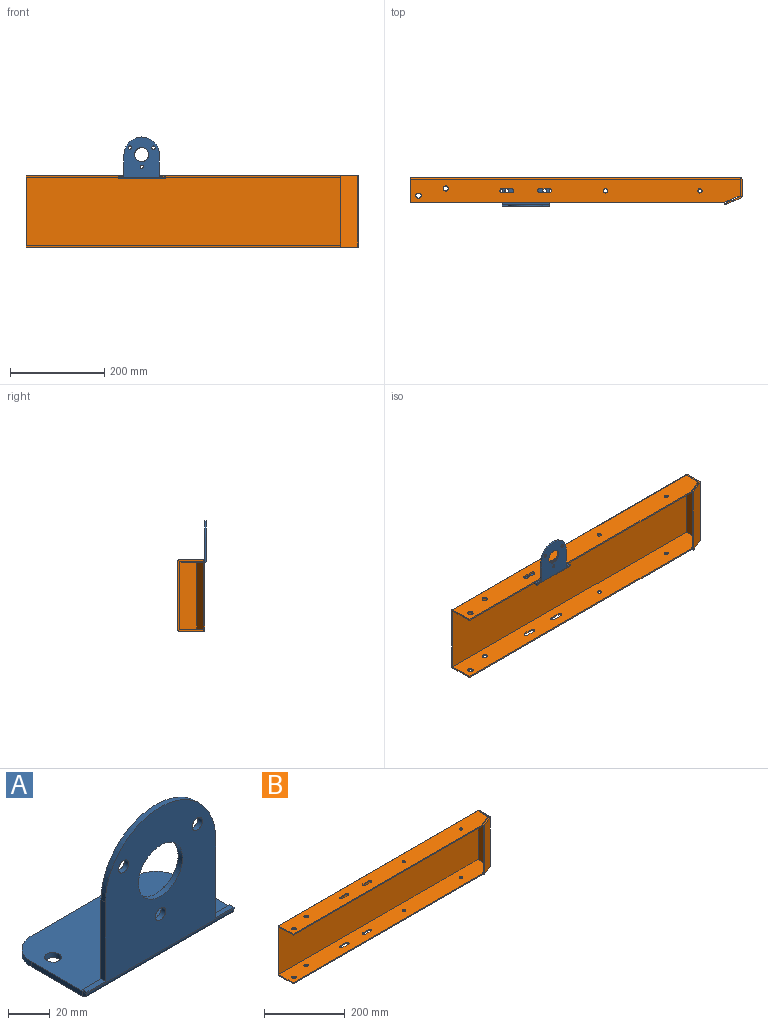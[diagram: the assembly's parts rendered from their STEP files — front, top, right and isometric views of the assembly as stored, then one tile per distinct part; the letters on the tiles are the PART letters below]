
ASSEMBLY  parts=2 mates=1
PART A: 26 faces, bbox 100x53x88 mm
  f0: plane 12.5x3mm, normal (0,0,1), area 37.5mm2, adj f1,f10,f11,f12
  f1: plane 3x0.99mm, normal (-1,0,0), area 3mm2, adj f0,f11,f12,f23
  f2: plane 3x0.99mm, normal (1,0,0), area 3mm2, adj f3,f11,f12,f22
  f3: plane 12.5x3mm, normal (0,0,1), area 37.5mm2, adj f2,f4,f11,f12
  f4: plane 46.5x3mm, normal (1,0,0), area 139.5mm2, adj f3,f5,f11,f12
  f5: cylinder r=37.5mm len=75mm, axis (0,-1,0), area 353.4mm2, adj f4,f10,f11,f12
  f6: cylinder r=15mm len=30mm, axis (0,-1,0), area 282.7mm2, adj f11,f12
  f7: cylinder r=3.5mm len=7mm, axis (0,-1,0), area 66mm2, adj f11,f12
  f8: cylinder r=3.5mm len=7mm, axis (0,-1,0), area 66mm2, adj f11,f12
  f9: cylinder r=3.5mm len=7mm, axis (0,-1,0), area 66mm2, adj f11,f12
  f10: plane 46.5x3mm, normal (-1,0,0), area 139.5mm2, adj f0,f5,f11,f12
  f11: plane 100x84.99mm, normal (0,-1,0), area 4973.1mm2, adj f0,f1,f2,f3,f4,f5,f6,f7
  f12: plane 100x84.99mm, normal (0,1,0), area 4973.1mm2, adj f0,f1,f2,f3,f4,f5,f6,f7
  f13: plane 70x3mm, normal (0,1,0), area 210mm2, adj f18,f19,f20,f21
  f14: plane 34.99x3mm, normal (1,0,0), area 105mm2, adj f18,f19,f20,f22
  f15: cylinder r=4mm len=8mm, axis (0,0,-1), area 75.4mm2, adj f18,f19
  f16: cylinder r=4mm len=8mm, axis (0,0,-1), area 75.4mm2, adj f18,f19
  f17: plane 34.99x3mm, normal (-1,0,0), area 105mm2, adj f18,f19,f21,f23
  f18: plane 100x49.99mm, normal (0,0,-1), area 4801.9mm2, adj f13,f14,f15,f16,f17,f20,f21,f24
  f19: plane 100x49.99mm, normal (0,0,1), area 4801.9mm2, adj f13,f14,f15,f16,f17,f20,f21,f25
  f20: cylinder r=15mm len=15mm, axis (0,0,-1), area 70.7mm2, adj f13,f14,f18,f19
  f21: cylinder r=15mm len=15mm, axis (0,0,-1), area 70.7mm2, adj f13,f17,f18,f19
  f22: plane 3.01x3.01mm, normal (1,0,0), area 7.1mm2, adj f2,f14,f24,f25
  f23: plane 3.01x3.01mm, normal (-1,0,0), area 7.1mm2, adj f1,f17,f24,f25
  f24: cylinder r=3.01mm len=100mm, axis (1,0,0), area 472.8mm2, adj f11,f18,f22,f23
  f25: cylinder r=0.01mm len=100mm, axis (1,0,0), area 1.6mm2, adj f12,f19,f22,f23
PART B: 70 faces, bbox 703x57.6x151 mm
  f0: plane 144.98x3mm, normal (-1,0,0), area 434.9mm2, adj f3,f4,f44,f67
  f1: plane 3x0.99mm, normal (0,0,1), area 3mm2, adj f3,f4,f22,f66
  f2: plane 3x0.99mm, normal (0,0,-1), area 3mm2, adj f3,f4,f23,f45
  f3: plane 699.99x144.98mm, normal (0,1,0), area 101484.6mm2, adj f0,f1,f2,f24,f46,f68
  f4: plane 699.99x144.98mm, normal (0,-1,0), area 101484.6mm2, adj f0,f1,f2,f25,f47,f69
  f5: plane 3x0.01mm, normal (0,1,0), area 0mm2, adj f9,f11,f12,f23
  f6: plane 3x3mm, normal (0,1,0), area 9mm2, adj f7,f10,f11,f12
  f7: plane 36.98x3mm, normal (0,0,1), area 111mm2, adj f6,f11,f12,f18
  f8: plane 36.98x3mm, normal (0,0,-1), area 111mm2, adj f9,f11,f12,f19
  f9: plane 3x3mm, normal (0,1,0), area 9mm2, adj f5,f8,f11,f12
  f10: plane 3x0.01mm, normal (0,1,0), area 0mm2, adj f6,f11,f12,f22
  f11: plane 151x36.98mm, normal (1,0,0), area 5584.5mm2, adj f5,f6,f7,f8,f9,f10,f20,f24
  f12: plane 151x36.98mm, normal (-1,0,0), area 5584.5mm2, adj f5,f6,f7,f8,f9,f10,f21,f25
  f13: plane 151x2.76mm, normal (-0.92,-0.39,0), area 453mm2, adj f14,f15,f16,f17
  f14: plane 36.16x17.61mm, normal (0,0,-1), area 114mm2, adj f13,f16,f17,f19
  f15: plane 36.16x17.61mm, normal (0,0,1), area 114mm2, adj f13,f16,f17,f18
  f16: plane 151x34.99mm, normal (0.39,-0.92,0), area 5739.2mm2, adj f13,f14,f15,f20
  f17: plane 151x34.99mm, normal (-0.39,0.92,0), area 5739.2mm2, adj f13,f14,f15,f21
  f18: plane 3.01x2.77mm, normal (0,0,1), area 5.3mm2, adj f7,f15,f20,f21
  f19: plane 3.01x2.77mm, normal (0,0,-1), area 5.3mm2, adj f8,f14,f20,f21
  f20: cylinder r=3.01mm len=151mm, axis (0,0,1), area 531.5mm2, adj f11,f16,f18,f19
  f21: cylinder r=0.01mm len=151mm, axis (0,0,1), area 1.8mm2, adj f12,f17,f18,f19
  f22: plane 3.01x3.01mm, normal (0,0,1), area 7.1mm2, adj f1,f10,f24,f25
  f23: plane 3.01x3.01mm, normal (0,0,-1), area 7.1mm2, adj f2,f5,f24,f25
  f24: cylinder r=3.01mm len=144.98mm, axis (0,0,1), area 685.5mm2, adj f3,f11,f22,f23
  f25: cylinder r=0.01mm len=144.98mm, axis (0,0,1), area 2.3mm2, adj f4,f12,f22,f23
  f26: plane 20x3mm, normal (0,1,0), area 60mm2, adj f27,f41,f42,f43
  f27: cylinder r=4.5mm len=9mm, axis (0,0,-1), area 42.4mm2, adj f26,f28,f42,f43
  f28: plane 20x3mm, normal (0,-1,0), area 60mm2, adj f27,f41,f42,f43
  f29: plane 20x3mm, normal (0,-1,0), area 60mm2, adj f30,f40,f42,f43
  f30: cylinder r=4.5mm len=9mm, axis (0,0,-1), area 42.4mm2, adj f29,f31,f42,f43
  f31: plane 20x3mm, normal (0,1,0), area 60mm2, adj f30,f40,f42,f43
  f32: plane 664x3mm, normal (0,-1,0), area 1992mm2, adj f33,f39,f42,f43
  f33: plane 49.99x3mm, normal (-1,0,0), area 150mm2, adj f32,f42,f43,f44
  f34: plane 35x3mm, normal (1,0,0), area 105mm2, adj f39,f42,f43,f45
  f35: cylinder r=4.5mm len=9mm, axis (0,0,-1), area 84.8mm2, adj f42,f43
  f36: cylinder r=4.5mm len=9mm, axis (0,0,-1), area 84.8mm2, adj f42,f43
  f37: cylinder r=5.5mm len=11mm, axis (0,0,-1), area 103.7mm2, adj f42,f43
  f38: cylinder r=5.5mm len=11mm, axis (0,0,-1), area 103.7mm2, adj f42,f43
  f39: plane 35x14.99mm, normal (0.39,-0.92,0), area 114.2mm2, adj f32,f34,f42,f43
  f40: cylinder r=4.5mm len=9mm, axis (0,0,-1), area 42.4mm2, adj f29,f31,f42,f43
  f41: cylinder r=4.5mm len=9mm, axis (0,0,-1), area 42.4mm2, adj f26,f28,f42,f43
  f42: plane 699x49.99mm, normal (0,0,-1), area 33876.1mm2, adj f26,f27,f28,f29,f30,f31,f32,f33
  f43: plane 699x49.99mm, normal (0,0,1), area 33876.1mm2, adj f26,f27,f28,f29,f30,f31,f32,f33
  f44: plane 3.01x3.01mm, normal (-1,0,0), area 7.1mm2, adj f0,f33,f46,f47
  f45: plane 3.01x3.01mm, normal (1,0,0), area 7.1mm2, adj f2,f34,f46,f47
  f46: cylinder r=3.01mm len=699mm, axis (-1,0,0), area 3304.9mm2, adj f3,f42,f44,f45
  f47: cylinder r=0.01mm len=699mm, axis (-1,0,0), area 11mm2, adj f4,f43,f44,f45
  f48: plane 20x3mm, normal (0,-1,0), area 60mm2, adj f49,f63,f64,f65
  f49: cylinder r=4.5mm len=9mm, axis (0,0,1), area 42.4mm2, adj f48,f50,f64,f65
  f50: plane 20x3mm, normal (0,1,0), area 60mm2, adj f49,f63,f64,f65
  f51: plane 20x3mm, normal (0,-1,0), area 60mm2, adj f52,f62,f64,f65
  f52: cylinder r=4.5mm len=9mm, axis (0,0,1), area 42.4mm2, adj f51,f53,f64,f65
  f53: plane 20x3mm, normal (0,1,0), area 60mm2, adj f52,f62,f64,f65
  f54: plane 35x3mm, normal (1,0,0), area 105mm2, adj f61,f64,f65,f66
  f55: plane 49.99x3mm, normal (-1,0,0), area 150mm2, adj f56,f64,f65,f67
  f56: plane 664x3mm, normal (0,-1,0), area 1992mm2, adj f55,f61,f64,f65
  f57: cylinder r=4.5mm len=9mm, axis (0,0,1), area 84.8mm2, adj f64,f65
  f58: cylinder r=4.5mm len=9mm, axis (0,0,1), area 84.8mm2, adj f64,f65
  f59: cylinder r=5.5mm len=11mm, axis (0,0,1), area 103.7mm2, adj f64,f65
  f60: cylinder r=5.5mm len=11mm, axis (0,0,1), area 103.7mm2, adj f64,f65
  f61: plane 35x14.99mm, normal (0.39,-0.92,0), area 114.2mm2, adj f54,f56,f64,f65
  f62: cylinder r=4.5mm len=9mm, axis (0,0,1), area 42.4mm2, adj f51,f53,f64,f65
  f63: cylinder r=4.5mm len=9mm, axis (0,0,1), area 42.4mm2, adj f48,f50,f64,f65
  f64: plane 699x49.99mm, normal (0,0,1), area 33876.1mm2, adj f48,f49,f50,f51,f52,f53,f54,f55
  f65: plane 699x49.99mm, normal (0,0,-1), area 33876.1mm2, adj f48,f49,f50,f51,f52,f53,f54,f55
  f66: plane 3.01x3.01mm, normal (1,0,0), area 7.1mm2, adj f1,f54,f68,f69
  f67: plane 3.01x3.01mm, normal (-1,0,0), area 7.1mm2, adj f0,f55,f68,f69
  f68: cylinder r=3.01mm len=699mm, axis (1,0,0), area 3304.9mm2, adj f3,f64,f66,f67
  f69: cylinder r=0.01mm len=699mm, axis (1,0,0), area 11mm2, adj f4,f65,f66,f67
PLACE A t=(-90.03,40.88,127.12)mm
PLACE B t=(-284.96,95.64,-20.88)mm
MATE fastened A.f15 <-> B.f65  axis (0,0,1) through (-0.03,70.88,127.12)mm
